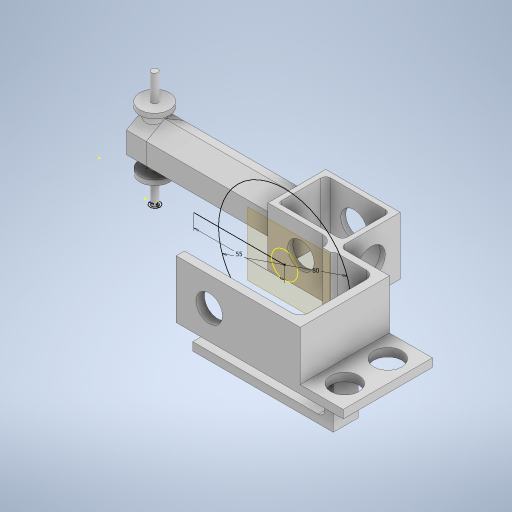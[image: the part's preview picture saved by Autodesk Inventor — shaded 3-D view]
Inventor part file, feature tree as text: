
AUTODESK INVENTOR PART (.ipt)
format: ipt  version: 2024 (Build 280153000, 153)  size: 647,168 bytes
history: native  units: in
note: dims shown in document units (in); Inventor stores cm internally (conversion verified against a paired STEP export)
features: sketch x27, extrude x25, fillet x11, plane x3
ambient origin geometry x8: Origin, YZ Plane, XZ Plane, XY Plane, X Axis, Y Axis, Z Axis, Center Point
bodies: Solid1 (feature_tree)
feature tree (66):
  extrude  "Extrusion1"  Depth=0.0984in
  extrude  "Extrusion2"  Depth=0.0787in TaperAngle=0.0deg
  extrude  "Extrusion3"  Depth=0.0787in TaperAngle=0.0deg
  extrude  "Extrusion4"  Depth=2.7559in
  fillet  "Fillet1"  Radius=2.7559in
  fillet  "Fillet2"  Radius=0.1969in
  extrude  "Extrusion5"  Depth=0.0984in
  extrude  "Extrusion6"  Depth=1.378in
  extrude  "Extrusion7"  Depth=1.378in TaperAngle=0.0deg
  extrude  "Extrusion8"  Depth=0.1181in
  extrude  "Extrusion9"  Depth=0.1181in TaperAngle=0.0deg
  fillet  "Fillet3"  Radius=0.6693in
  fillet  "Fillet4"  Radius=0.1181in
  plane  "Work Plane1"
  sketch  "Sketch11"  dims[d30=0.9843in d31=0.6299in]
  extrude  "Extrusion15"  Depth=0.6299in
  extrude  "Extrusion18"  Depth=0.1181in
  extrude  "Extrusion19"  Depth=0.3937in
  extrude  "Extrusion20"  Depth=2.1654in
  extrude  "Extrusion21"  Depth=0.3937in
  extrude  "Extrusion22"  Depth=1.378in TaperAngle=0.0deg
  extrude  "Extrusion23"  Depth=0.1575in
  extrude  "Extrusion24"  Depth=0.1969in
  extrude  "Extrusion25"  Depth=0.1969in
  extrude  "Extrusion26"  Depth=2.7559in
  fillet  "Fillet9"  Radius=0.5906in
  fillet  "Fillet10"  Radius=1.1811in
  fillet  "Fillet11"  Radius=0.1969in
  fillet  "Fillet12"  Radius=0.1969in
  fillet  "Fillet13"  Radius=3.1496in
  fillet  "Fillet14"  Radius=0.1969in
  fillet  "Fillet15"  Radius=1.0236in
  plane  "Work Plane2"
  extrude  "Extrusion27"  Depth=0.6693in
  plane  "Work Plane3"
  extrude  "Extrusion28"  Depth=11.811in TaperAngle=0.0deg
  extrude  "Extrusion29"  Depth=0.1181in
  extrude  "Extrusion30"  Depth=0.1969in
  sketch  "Sketch35"  dims[d118=0.1575in d119=-0.748in]
  extrude  "Extrusion31"  Depth=0.1575in
  extrude  "Extrusion32"  [1 undecoded]
  sketch  "Sketch1"  dims[d0=0.3937in d1=0.0984in]
  sketch  "Sketch2"  dims[d2=0.3937in d3=0.0in d4=0.0787in d5=0.0in]
  sketch  "Sketch3"  dims[d6=0.3937in d7=0.0787in d8=0.0in]
  sketch  "Sketch4"  dims[d9=0.2362in d10=0.1969in d11=2.7559in d12=0.0in d13=0.1969in]
  sketch  "Sketch5"  dims[d14=0.1575in d15=0.0984in]
  sketch  "Sketch6"  dims[d16=3.1496in d17=0.0in d18=1.378in]
  sketch  "Sketch8"  dims[d19=1.378in d20=1.7717in d21=0.0in]
  sketch  "Sketch9"  dims[d22=0.1181in d23=0.1181in]
  sketch  "Sketch10"  dims[d24=0.1181in d25=1.7717in d26=0.0in d27=0.6693in d28=0.1181in d29=0.0in]
  sketch  "Sketch19"  dims[d32=1.378in d33=0.0in d34=0.1181in]
  sketch  "Sketch22"  dims[d35=0.0787in d36=0.3937in]
  sketch  "Sketch23"  dims[d37=3.1496in d38=2.1654in]
  sketch  "Sketch24"  dims[d72=0.3937in d73=0.0in d80=0.2756in]
  sketch  "Sketch25"  dims[d81=1.378in d82=0.1969in d83=0.0in]
  sketch  "Sketch26"  dims[d84=0.1378in d85=0.1575in]
  sketch  "Sketch27"  dims[d86=1.1811in d87=0.0in d88=0.1969in]
  sketch  "Sketch28"  dims[d89=1.9685in d90=0.0in d91=0.1969in]
  sketch  "Sketch29"  dims[d92=2.7559in d93=0.0in d95=0.2953in d96=0.5906in d97=1.1811in d98=0.1969in d99=0.0in d100=0.1969in d101=3.1496in d102=0.0in d103=0.1969in d104=1.0236in d105=0.0in]
  sketch  "Sketch30"  dims[d106=0.5118in d107=0.6693in]
  sketch  "Sketch31"  dims[d108=1.0236in d109=0.0in d110=11.811in d111=0.0in]
  sketch  "Sketch32"  dims[d112=0.1181in d113=0.1181in]
  sketch  "Sketch33"  dims[d114=0.2677in d115=0.1969in]
  sketch  "Sketch34"  dims[d116=0.1969in d117=0.1575in]
  sketch  "Sketch36"  dims[d120=0.315in]
  sketch  "Sketch37"  dims[d121=0.1181in d122=0.0in d123=-0.748in d124=0.1181in d125=0.0in d126=0.1575in d127=3.937in d128=0.0in d129=0.7087in d130=0.1181in d131=0.0in d132=0.1575in d133=0.2362in d134=0.1575in d135=0.2362in d136=0.6299in d137=0.0in d138=0.7087in d139=0.1181in d140=0.0in d39=0.0in d74=0.0197in d75=0.0344in]
note: 1 required parameter value undecoded (feature->parameter linkage not recoverable at this tier; creation-order binding heuristic only, values carry confidence <= 0.55)
